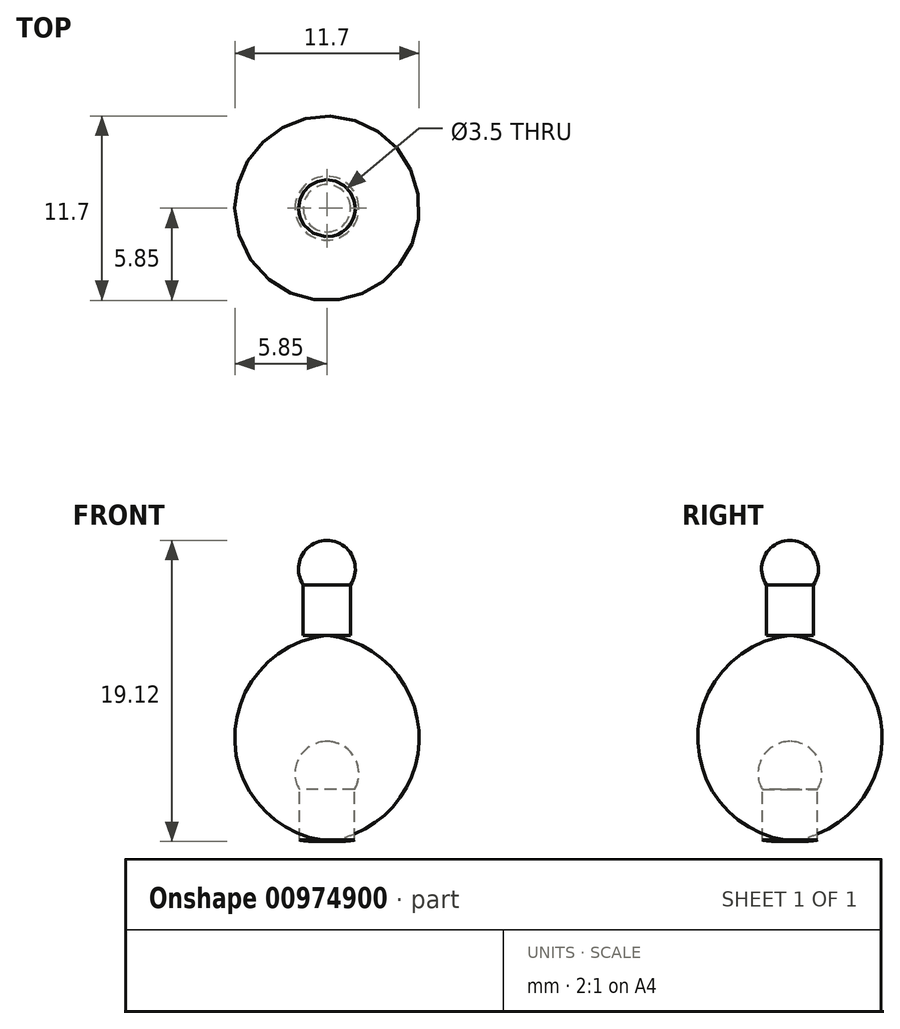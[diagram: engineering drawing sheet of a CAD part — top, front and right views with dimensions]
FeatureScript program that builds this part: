
annotation { "Feature Type Name" : "Feature", "Feature Type Description" : "" }
export const myFeature = defineFeature(function(context is Context, id is Id, definition is map)
    precondition{}
    {
        {
            var Q0;
            Q0=qCreatedBy(makeId("Front.planeOp"),FACE);
            var sketch = newSketch(context, id + "F0", { "sketchPlane" : qUnion([Q0])});
            skLineSegment(sketch, "E0", {"start": v(0, 0) * mm, "end": v(0, 9.04) * mm, "construction": true});
            skLineSegment(sketch, "E1", {"start": v(0, 0) * mm, "end": v(0, -9.99) * mm, "construction": true});
            skLineSegment(sketch, "E2", {"start": v(0, 5.87) * mm, "end": v(8.32, 5.87) * mm, "construction": true});
            skLineSegment(sketch, "E3", {"start": v(0, -7.13) * mm, "end": v(9.52, -7.13) * mm, "construction": true});
            skArc(sketch, "E4", {"start": v(1.75, -7.13) * mm, "mid": v(7.28, -0.52) * mm, "end": v(1.5, 5.87) * mm});
            skLineSegment(sketch, "E5", {"start": v(1.75, -7.13) * mm, "end": v(1.75, -3.91) * mm});
            skArc(sketch, "E6", {"start": v(1.75, -3.91) * mm, "mid": v(1.76, -1.88) * mm, "end": v(0, -0.86) * mm});
            skLineSegment(sketch, "E7", {"start": v(1.5, 5.87) * mm, "end": v(1.5, 9.09) * mm});
            skArc(sketch, "E8", {"start": v(1.5, 9.09) * mm, "mid": v(1.6, 10.94) * mm, "end": v(0, 11.9) * mm});
            skLineSegment(sketch, "E9", {"start": v(0, 11.9) * mm, "end": v(0, -0.86) * mm});
            skSolve(sketch);
        }
        {
            var Q0;
            Q0 = qSketchRegion(id + "F0", true);
            var Q1;
            Q1=sQuery(id+"F0.wireOp",EDGE,"E1");
            revolve(context, id + "F1", {"surfaceOperationType" : NewSurfaceOperationType.NEW, "entities" : qUnion([Q0]), "axis" : qUnion([Q1]), "revolveType" : RevolveType.FULL});
        }
    });
